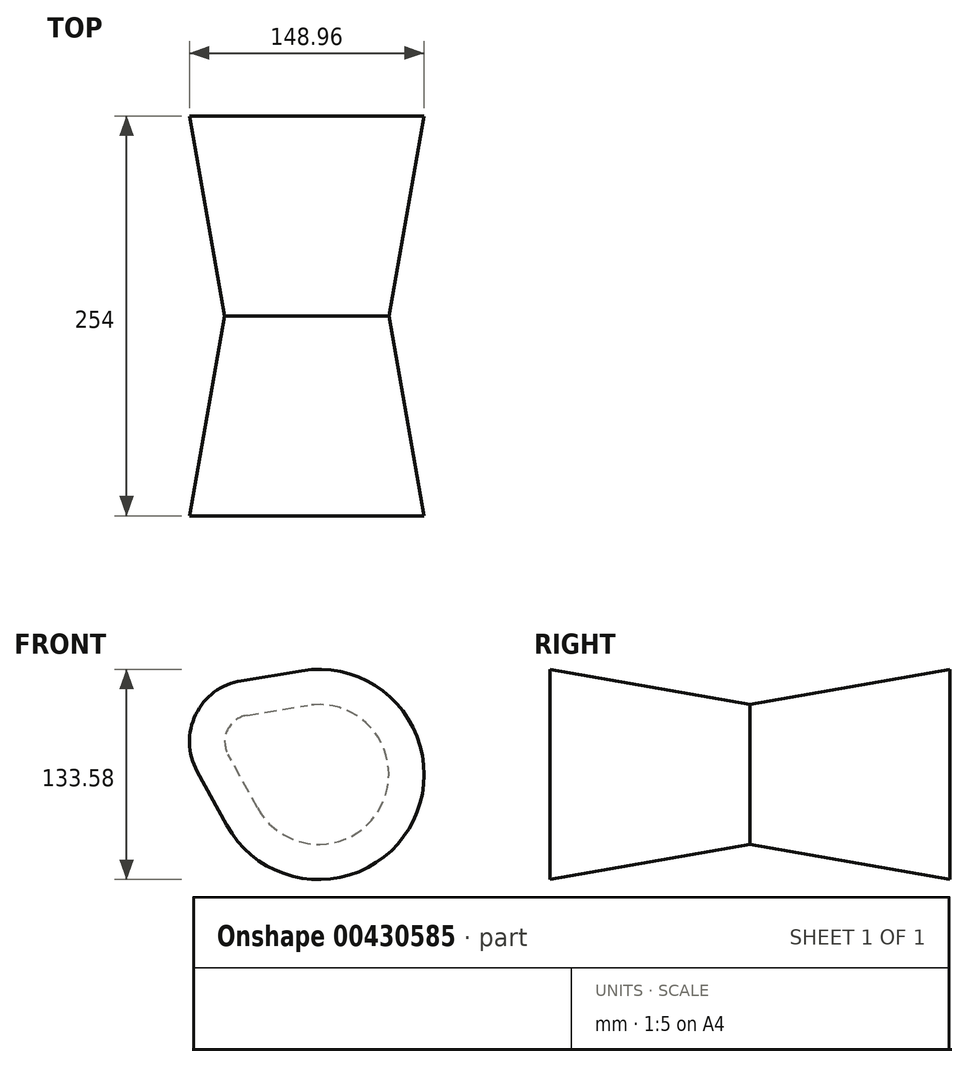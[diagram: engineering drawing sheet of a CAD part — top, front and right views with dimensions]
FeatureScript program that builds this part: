
annotation { "Feature Type Name" : "Feature", "Feature Type Description" : "" }
export const myFeature = defineFeature(function(context is Context, id is Id, definition is map)
    precondition{}
    {
        {
            var Q0;
            Q0=qCreatedBy(makeId("Front.planeOp"),FACE);
            var sketch = newSketch(context, id + "F0", { "sketchPlane" : qUnion([Q0])});
            skArc(sketch, "E0", {"start": v(-29.08, 25.65) * mm, "mid": v(-41.42, 16.44) * mm, "end": v(-41.04, 1.04) * mm});
            skArc(sketch, "E1", {"start": v(-22.25, -33.18) * mm, "mid": v(56.59, -31.22) * mm, "end": v(9.44, 32) * mm});
            skLineSegment(sketch, "E2", {"start": v(-29.08, 25.65) * mm, "end": v(9.44, 32) * mm});
            skLineSegment(sketch, "E3", {"start": v(-41.04, 1.04) * mm, "end": v(-22.25, -33.18) * mm});
            skSolve(sketch);
        }
        {
            var Q0;
            Q0 = qSketchRegion(id + "F0", true);
            extrude(context, id + "F1", {"entities" : qUnion([Q0]), "depth" : 254 * mm, "hasDraft" : true, "draftAngle" : 10 * degree, "symmetric" : true});
        }
    });
